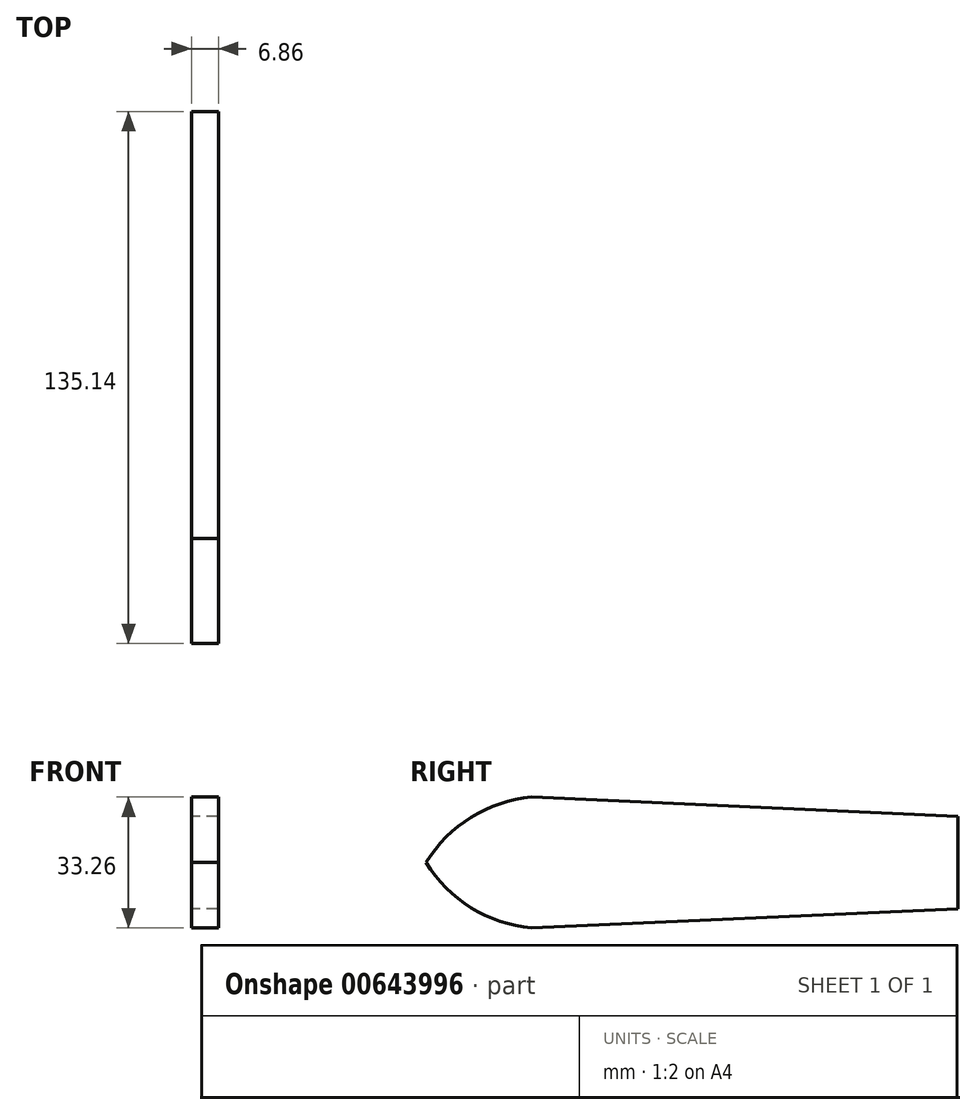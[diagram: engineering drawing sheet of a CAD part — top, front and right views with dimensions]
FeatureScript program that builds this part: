
annotation { "Feature Type Name" : "Feature", "Feature Type Description" : "" }
export const myFeature = defineFeature(function(context is Context, id is Id, definition is map)
    precondition{}
    {
        {
            var Q0;
            Q0=qCreatedBy(makeId("Right.planeOp"),FACE);
            var sketch = newSketch(context, id + "F0", { "sketchPlane" : qUnion([Q0])});
            skArc(sketch, "E0", {"start": v(-47.33, 16.63) * mm, "mid": v(-62.67, 11.47) * mm, "end": v(-74.08, 0) * mm});
            skLineSegment(sketch, "E1", {"start": v(-74.08, 0) * mm, "end": v(61.06, 0) * mm});
            skLineSegment(sketch, "E2", {"start": v(61.06, 0) * mm, "end": v(61.06, 11.75) * mm});
            skLineSegment(sketch, "E3", {"start": v(61.06, 11.75) * mm, "end": v(-47.33, 16.63) * mm});
            skLineSegment(sketch, "E4.MirrorCS", {"start": v(61.06, -11.75) * mm, "end": v(-47.33, -16.63) * mm});
            skArc(sketch, "E5.MirrorCS", {"start": v(-47.33, -16.63) * mm, "mid": v(-62.67, -11.47) * mm, "end": v(-74.08, 0) * mm});
            skLineSegment(sketch, "E6.MirrorCS", {"start": v(61.06, 0) * mm, "end": v(61.06, -11.75) * mm});
            skSolve(sketch);
        }
        {
            var Q0;
            Q0=makeQuery(id+"F0.imprint","IMPRINT",FACE,{"disambiguationData":[TD([[makeQuery(id+"F0.imprint","IMPRINT",EDGE,{"derivedFrom":sQuery(id+"F0.wireOp",EDGE,"E0")}),1.0]])]});
            var Q1;
            Q1=makeQuery(id+"F0.imprint","IMPRINT",FACE,{"disambiguationData":[TD([[makeQuery(id+"F0.imprint","IMPRINT",EDGE,{"derivedFrom":sQuery(id+"F0.wireOp",EDGE,"E1")}),-1.0]])]});
            extrude(context, id + "F1", {"entities" : qUnion([Q0, Q1]), "depth" : 6.86 * mm, "offsetDistance" : 25.4 * mm});
        }
        {
            var Q0;
            Q0=makeQuery(id+"F1.opExtrude","SWEPT_FACE",FACE,{"disambiguationData":[OSD([sQuery(id+"F0.wireOp",EDGE,"E2"),sQuery(id+"F0.wireOp",EDGE,"E6.MirrorCS")])]});
            var sketch = newSketch(context, id + "F2", { "sketchPlane" : qUnion([Q0])});
            skArc(sketch, "E7", {"start": v(-5.72, 0) * mm, "mid": v(-4.04, 4.04) * mm, "end": v(0, 5.72) * mm});
            skPoint(sketch, "E7.startSnap0", {"position": v(0, 0) * mm});
            skArc(sketch, "E8", {"start": v(0, -5.69) * mm, "mid": v(-4.02, -4.02) * mm, "end": v(-5.69, 0) * mm});
            skLineSegment(sketch, "E9", {"start": v(0, 5.72) * mm, "end": v(0, -5.69) * mm});
            skSolve(sketch);
        }
        {
            var Q0;
            {var subQ4=sQuery(id+"F2.wireOp",EDGE,"E9");Q0=makeQuery(id+"F2.imprint","IMPRINT",FACE,{"disambiguationData":[TD([[makeQuery(id+"F2.imprint","IMPRINT",EDGE,{"derivedFrom":subQ4}),1.0]])]});}
            var Q1;
            Q1=sQuery(id+"F2.wireOp",EDGE,"E7");
            var Q2;
            Q2=sQuery(id+"F2.wireOp",EDGE,"E9");
            var Q3;
            Q3=sQuery(id+"F2.wireOp",EDGE,"E8");
            extrude(context, id + "F3", {"entities" : qUnion([Q0]), "bodyType" : ToolBodyType.SURFACE, "operationType" : NewBodyOperationType.ADD, "surfaceEntities" : qUnion([Q1, Q2, Q3]), "oppositeDirection" : true, "depth" : 25.1 * mm, "offsetDistance" : 25.4 * mm});
        }
        {
            var Q0;
            Q0=makeQuery(id+"F1.opExtrude","CAP_FACE",FACE,{"disambiguationData":[OSD([sQuery(id+"F0.wireOp",EDGE,"E0"),sQuery(id+"F0.wireOp",EDGE,"E2"),sQuery(id+"F0.wireOp",EDGE,"E3"),sQuery(id+"F0.wireOp",EDGE,"E4.MirrorCS"),sQuery(id+"F0.wireOp",EDGE,"E5.MirrorCS"),sQuery(id+"F0.wireOp",EDGE,"E6.MirrorCS")])],"isStart":false});
            cPlane(context, id + "F4", {"entities" : qUnion([Q0]), "cplaneType" : CPlaneType.OFFSET, "offset" : 0 * mm, "width" : 152.4 * mm, "height" : 152.4 * mm});
        }
    });
